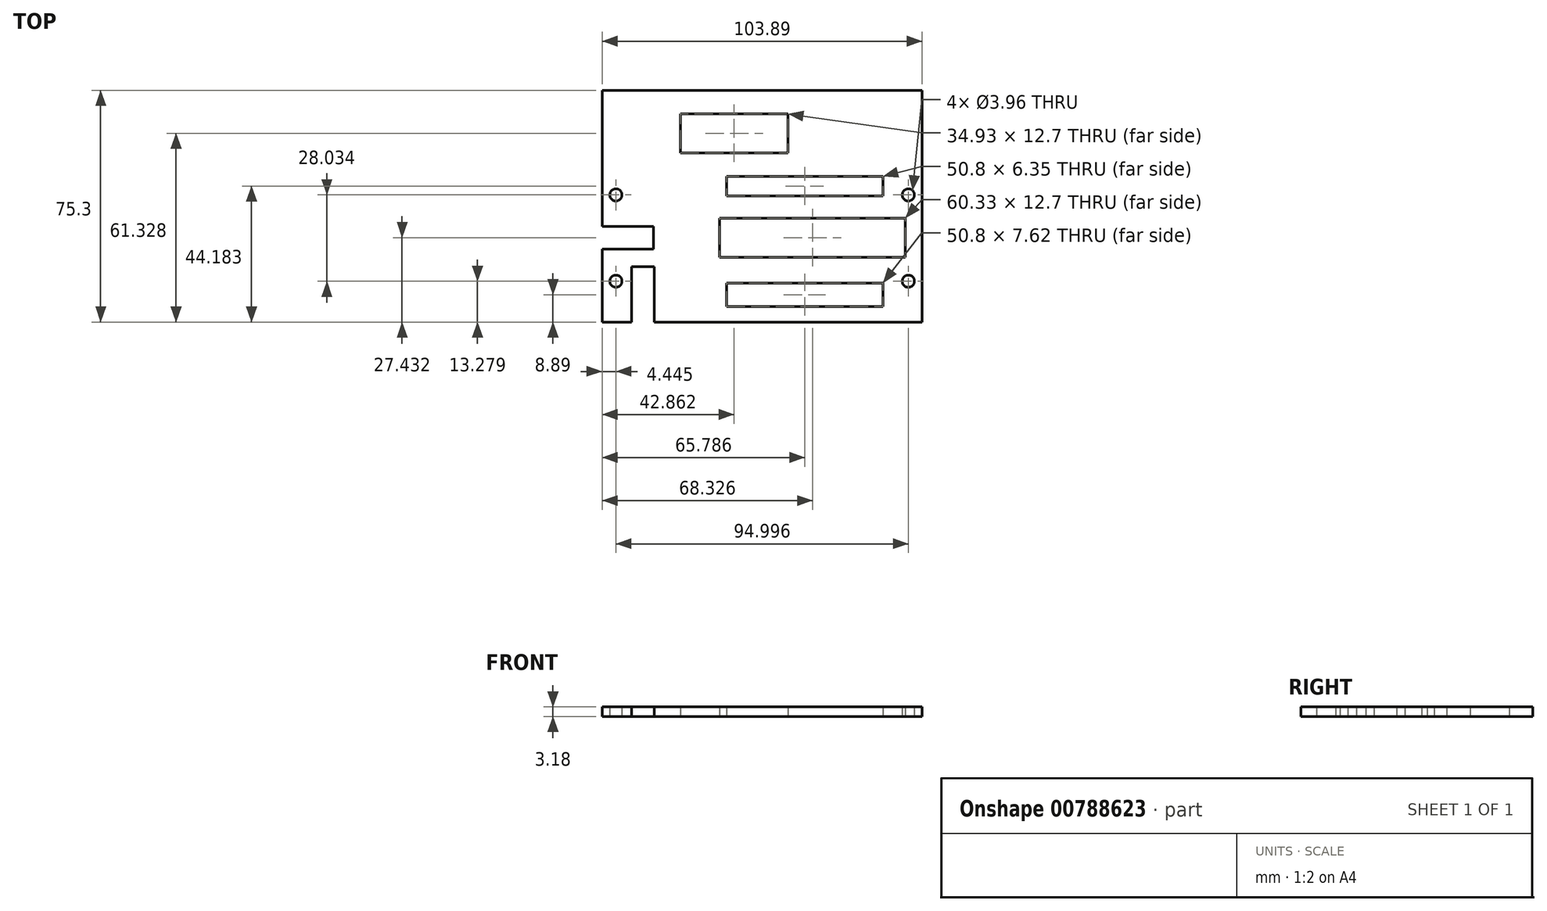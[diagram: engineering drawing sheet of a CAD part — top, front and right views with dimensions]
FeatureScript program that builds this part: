
annotation { "Feature Type Name" : "Feature", "Feature Type Description" : "" }
export const myFeature = defineFeature(function(context is Context, id is Id, definition is map)
    precondition{}
    {
        {
            var Q0;
            Q0=qCreatedBy(makeId("Top.planeOp"),FACE);
            var sketch = newSketch(context, id + "F0", { "sketchPlane" : qUnion([Q0])});
            skLineSegment(sketch, "E0.bottom", {"start": v(0, 0) * mm, "end": v(103.89, 0) * mm});
            skLineSegment(sketch, "E0.top", {"start": v(0, 75.3) * mm, "end": v(103.89, 75.3) * mm});
            skLineSegment(sketch, "E0.left", {"start": v(0, 0) * mm, "end": v(0, 75.3) * mm});
            skLineSegment(sketch, "E0.right", {"start": v(103.89, 0) * mm, "end": v(103.89, 75.3) * mm});
            skLineSegment(sketch, "E1.bottom", {"start": v(9.52, 0) * mm, "end": v(16.89, 0) * mm});
            skLineSegment(sketch, "E1.top", {"start": v(9.52, 18.03) * mm, "end": v(16.89, 18.03) * mm});
            skLineSegment(sketch, "E1.left", {"start": v(9.52, 0) * mm, "end": v(9.52, 18.03) * mm});
            skLineSegment(sketch, "E1.right", {"start": v(16.89, 0) * mm, "end": v(16.89, 18.03) * mm});
            skLineSegment(sketch, "E2.bottom", {"start": v(0, 31.1) * mm, "end": v(16.64, 31.1) * mm});
            skLineSegment(sketch, "E2.top", {"start": v(0, 23.74) * mm, "end": v(16.64, 23.74) * mm});
            skLineSegment(sketch, "E2.left", {"start": v(0, 31.1) * mm, "end": v(0, 23.74) * mm});
            skLineSegment(sketch, "E2.right", {"start": v(16.64, 31.1) * mm, "end": v(16.64, 23.74) * mm});
            skLineSegment(sketch, "E3.bottom", {"start": v(25.4, 67.68) * mm, "end": v(60.32, 67.68) * mm});
            skLineSegment(sketch, "E3.top", {"start": v(25.4, 54.98) * mm, "end": v(60.32, 54.98) * mm});
            skLineSegment(sketch, "E3.left", {"start": v(25.4, 67.68) * mm, "end": v(25.4, 54.98) * mm});
            skLineSegment(sketch, "E3.right", {"start": v(60.32, 67.68) * mm, "end": v(60.32, 54.98) * mm});
            skLineSegment(sketch, "E4.bottom", {"start": v(40.39, 47.36) * mm, "end": v(91.19, 47.36) * mm});
            skLineSegment(sketch, "E4.top", {"start": v(40.39, 41) * mm, "end": v(91.19, 41) * mm});
            skLineSegment(sketch, "E4.left", {"start": v(40.39, 47.36) * mm, "end": v(40.39, 41) * mm});
            skLineSegment(sketch, "E4.right", {"start": v(91.19, 47.36) * mm, "end": v(91.19, 41) * mm});
            skLineSegment(sketch, "E5.bottom", {"start": v(38.16, 33.78) * mm, "end": v(98.49, 33.78) * mm});
            skLineSegment(sketch, "E5.top", {"start": v(38.16, 21.08) * mm, "end": v(98.49, 21.08) * mm});
            skLineSegment(sketch, "E5.left", {"start": v(38.16, 33.78) * mm, "end": v(38.16, 21.08) * mm});
            skLineSegment(sketch, "E5.right", {"start": v(98.49, 33.78) * mm, "end": v(98.49, 21.08) * mm});
            skLineSegment(sketch, "E6.bottom", {"start": v(40.39, 12.7) * mm, "end": v(91.19, 12.7) * mm});
            skLineSegment(sketch, "E6.top", {"start": v(40.39, 5.08) * mm, "end": v(91.19, 5.08) * mm});
            skLineSegment(sketch, "E6.left", {"start": v(40.39, 12.7) * mm, "end": v(40.39, 5.08) * mm});
            skLineSegment(sketch, "E6.right", {"start": v(91.19, 12.7) * mm, "end": v(91.19, 5.08) * mm});
            skCircle(sketch, "E7", {"center": v(99.44, 13.28) * mm, "radius": 1.98 * mm});
            skCircle(sketch, "E8", {"center": v(99.44, 41.31) * mm, "radius": 1.98 * mm});
            skCircle(sketch, "E9", {"center": v(4.44, 41.31) * mm, "radius": 1.98 * mm});
            skCircle(sketch, "E10", {"center": v(4.45, 13.28) * mm, "radius": 1.98 * mm});
            skSolve(sketch);
        }
        {
            var Q0;
            {var subQ5=sQuery(id+"F0.wireOp",EDGE,"E0.top");Q0=makeQuery(id+"F0.imprint","IMPRINT",FACE,{"disambiguationData":[TD([[makeQuery(id+"F0.imprint","IMPRINT",EDGE,{"derivedFrom":subQ5}),-1.0]])]});}
            extrude(context, id + "F1", {"entities" : qUnion([Q0]), "depth" : 3.17 * mm, "offsetDistance" : 25.4 * mm});
        }
    });
